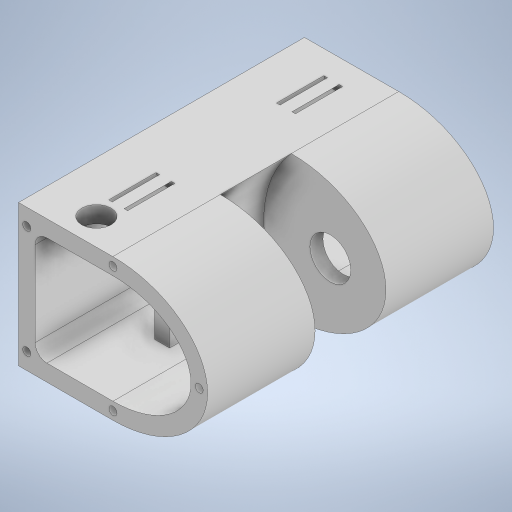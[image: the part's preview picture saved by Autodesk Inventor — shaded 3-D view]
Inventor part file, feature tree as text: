
AUTODESK INVENTOR PART (.ipt)
format: ipt  version: 2024 (Build 280153000, 153)  size: 1,189,376 bytes
history: native  units: in
note: dims shown in document units (in); Inventor stores cm internally (conversion verified against a paired STEP export)
features: sketch x23, extrude x21, projected_geometry x7, plane x4, other x2, thicken_offset x1, mirror x1, boolean_combine x1
ambient origin geometry x8: Origin, YZ Plane, XZ Plane, XY Plane, X Axis, Y Axis, Z Axis, Center Point
bodies: Solid1 (feature_tree), Solid2 (feature_tree)
feature tree (60):
  extrude  "Extrusion1"  Depth=0.8in TaperAngle=180.0deg
  extrude  "Extrusion2"  Depth=0.35in
  extrude  "Extrusion3"  Depth=2.0in TaperAngle=0.0deg
  extrude  "Extrusion4"  Depth=0.8736in
  thicken_offset  "Thicken1"
  extrude  "Extrusion7"  Depth=0.75in
  sketch  "Sketch10"  dims[d38=0.35in d39=0.17in]
  extrude  "Extrusion9"  Depth=0.25in
  plane  "Work Plane4"
  plane  "Work Plane5"
  mirror  "Mirror5"
  boolean_combine  "Combine2"
  extrude  "Extrusion11"  Depth=0.35in
  extrude  "Extrusion12"  Depth=0.175in
  plane  "Work Plane6"
  plane  "Work Plane7"
  extrude  "Extrusion18"  Depth=0.32in
  extrude  "Extrusion19"  Depth=1.2in
  extrude  "Extrusion20"  Depth=0.425in TaperAngle=0.0deg
  extrude  "Extrusion21"  Depth=1.0in TaperAngle=0.0deg
  extrude  "Extrusion22"  Depth=0.35in
  extrude  "Extrusion23"  Depth=0.35in
  sketch  "Sketch30"  dims[d115=2.725in d116=0.0in d118=-1.0in]
  extrude  "Extrusion24"  [1 undecoded]
  extrude  "Extrusion25"  Depth=2.725in TaperAngle=0.0deg
  extrude  "Extrusion26"  [1 undecoded]
  extrude  "Extrusion27"  Depth=0.075in
  extrude  "Extrusion28"  Depth=1.0in TaperAngle=0.0deg
  sketch  "Sketch38"  dims[d156=0.6in d157=1.0in d158=0.0in d159=0.42in d160=1.0in d161=0.0in d162=0.75in d163=90.0deg d164=0.24in d165=0.18in d166=0.32in d167=0.0in d168=0.24in d170=0.17in d171=0.17in d175=0.0752in d181=0.28in d182=0.55in d183=0.0in d184=0.3825in d185=0.0in d186=0.62in d187=0.7in d188=0.0in d189=0.3825in d190=0.0in d191=1.0in d192=0.0in d193=1.0in d194=0.0in d195=0.5in d196=0.0in d199=1.8247in d201=0.17in d203=1.503in d204=0.175in d205=0.175in d206=0.35in d207=0.175in d208=0.175in d209=0.35in d210=1.8252in d211=3.825in]
  sketch  "Sketch1"  dims[d3=0.866in d4=0.8in d5=180.0deg d9=0.0in]
  sketch  "Sketch2"  dims[d10=0.0in d12=0.35in]
  projected_geometry  "Projected Loop1"
  sketch  "Sketch3"  dims[d14=1.7162in d16=2.0in d17=0.0in]
  sketch  "Sketch4"  dims[d18=0.866in d19=0.8736in]
  sketch  "Sketch8"  dims[d20=0.9in d21=0.75in]
  sketch  "Sketch9"  dims[d22=0.2755in d23=0.0in d29=0.25in]
  other  "Srf1"
  sketch  "Sketch14"  dims[d40=0.17in d50=0.175in]
  other  "Srf5"
  sketch  "Sketch16"  dims[d51=0.41in d52=0.0in d53=0.32in]
  sketch  "Sketch17"  dims[d54=0.416in d55=1.2in]
  sketch  "Sketch24"  dims[d56=0.32in d57=0.425in d58=0.0in]
  sketch  "Sketch25"  dims[d73=0.15in d74=1.0in d75=0.0in]
  projected_geometry  "Projected Loop10"
  sketch  "Sketch26"  dims[d76=0.75in d77=0.0in d78=0.35in]
  sketch  "Sketch27"  dims[d79=0.35in d98=0.2in]
  sketch  "Sketch28"  dims[d99=0.85in d100=0.0in d101=-1.0in]
  sketch  "Sketch29"  dims[d112=0.0in d113=2.725in d114=0.0in]
  projected_geometry  "Projected Loop11"
  sketch  "Sketch31"  dims[d119=-1.0in d145=0.075in]
  sketch  "Sketch32"  dims[d146=0.075in d147=1.0in d148=0.0in]
  sketch  "Sketch33"  dims[d149=1.0in d150=0.0in d151=0.62in]
  projected_geometry  "Projected Loop12"
  sketch  "Sketch34"  dims[d152=0.15in d153=1.0in d154=0.0in]
  projected_geometry  "Projected Loop13"
  sketch  "Sketch35"  dims[d155=1.5in]
  projected_geometry  "Projected Loop14"
  projected_geometry  "Projected Loop15"
  extrude  "ExtrusionSrf1"  Depth=0.62in
  extrude  "ExtrusionSrf5"  Depth=1.0in TaperAngle=0.0deg
note: 2 required parameter values undecoded (feature->parameter linkage not recoverable at this tier; creation-order binding heuristic only, values carry confidence <= 0.55)
